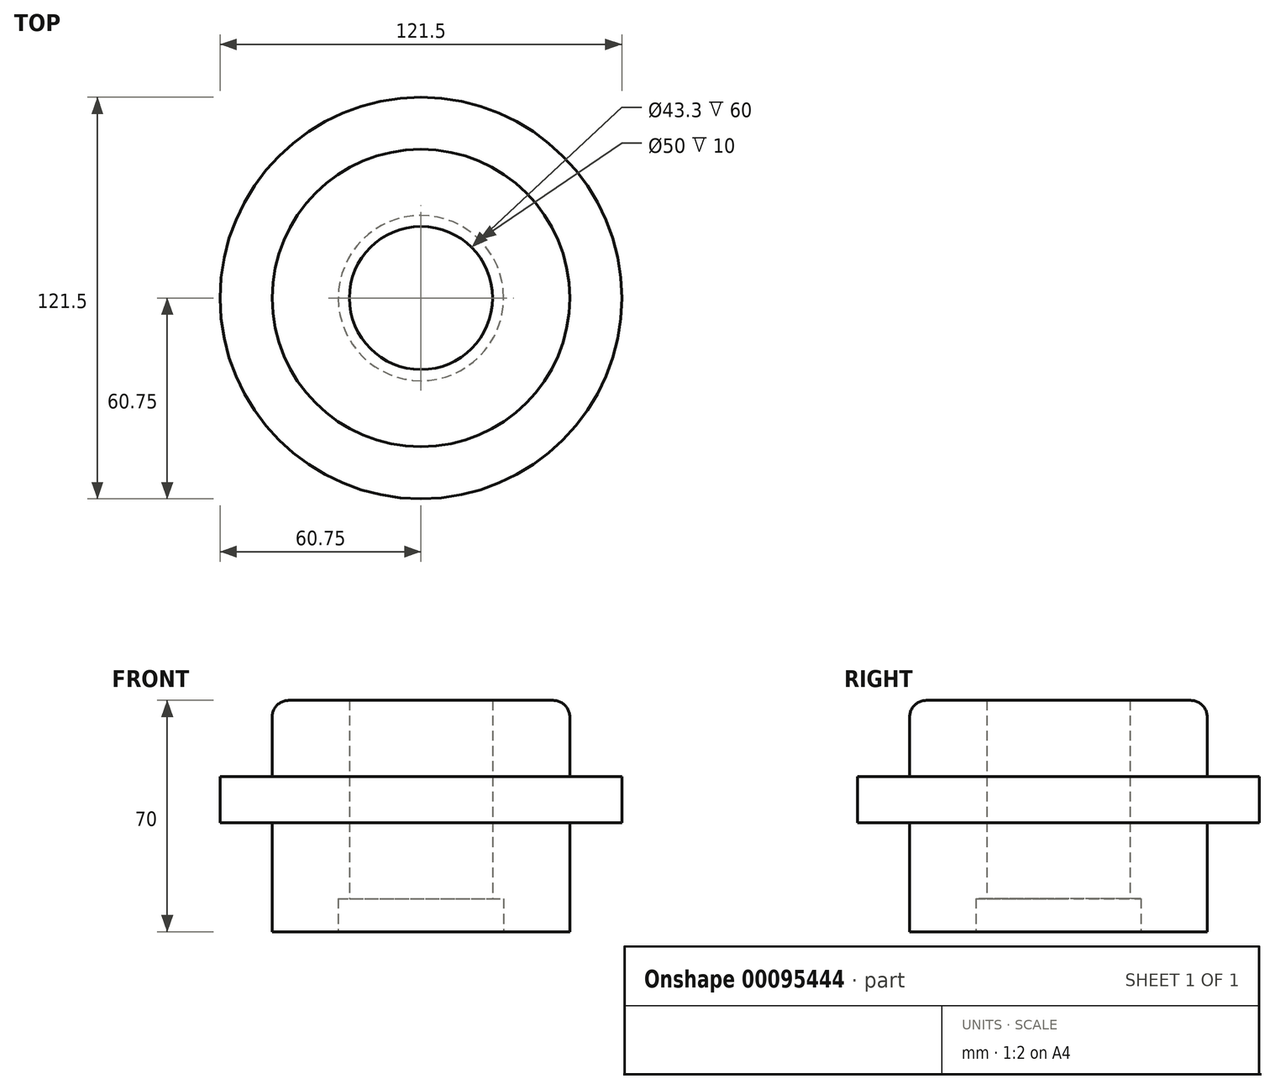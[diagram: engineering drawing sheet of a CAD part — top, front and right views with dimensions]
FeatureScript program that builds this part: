
annotation { "Feature Type Name" : "Feature", "Feature Type Description" : "" }
export const myFeature = defineFeature(function(context is Context, id is Id, definition is map)
    precondition{}
    {
        {
            var Q0;
            Q0=qCreatedBy(makeId("Front.planeOp"),FACE);
            var sketch = newSketch(context, id + "F0", { "sketchPlane" : qUnion([Q0])});
            skLineSegment(sketch, "E0", {"start": v(-60.75, 0) * mm, "end": v(-60.75, 14) * mm});
            skLineSegment(sketch, "E1", {"start": v(-60.75, 14) * mm, "end": v(-45, 14) * mm});
            skLineSegment(sketch, "E2", {"start": v(-45, 14) * mm, "end": v(-45, 37) * mm});
            skLineSegment(sketch, "E3", {"start": v(-45, 37) * mm, "end": v(-21.65, 37) * mm});
            skLineSegment(sketch, "E4", {"start": v(-21.65, 37) * mm, "end": v(-21.65, -33) * mm});
            skLineSegment(sketch, "E5", {"start": v(-21.65, -33) * mm, "end": v(-45, -33) * mm});
            skLineSegment(sketch, "E6", {"start": v(-45, -33) * mm, "end": v(-45, 0) * mm});
            skLineSegment(sketch, "E7", {"start": v(-45, 0) * mm, "end": v(-60.75, 0) * mm});
            skLineSegment(sketch, "E8", {"start": v(0, 0) * mm, "end": v(0, 56.62) * mm, "construction": true});
            skSolve(sketch);
        }
        {
            var Q0;
            Q0=makeQuery(id+"F0.imprint","IMPRINT",FACE,{"disambiguationData":[TD([[makeQuery(id+"F0.imprint","IMPRINT",EDGE,{"derivedFrom":sQuery(id+"F0.wireOp",EDGE,"E0")}),-1.0]])]});
            var Q1;
            Q1=sQuery(id+"F0.wireOp",EDGE,"E8");
            revolve(context, id + "F1", {"entities" : qUnion([Q0]), "axis" : qUnion([Q1]), "revolveType" : RevolveType.FULL});
        }
        {
            var Q0;
            Q0=makeQuery(id+"F1.opRevolve","SWEPT_EDGE",EDGE,{"disambiguationData":[OSD([sQuery(id+"F0.wireOp",EDGE,"E2"),sQuery(id+"F0.wireOp",EDGE,"E3")])]});
            fillet(context, id + "F2", {"entities" : qUnion([Q0]), "radius" : 5 * mm, "tangentPropagation" : true, "allowEdgeOverflow" : false});
        }
        {
            var Q0;
            Q0=makeQuery(id+"F1.opRevolve","SWEPT_FACE",FACE,{"disambiguationData":[OSD([sQuery(id+"F0.wireOp",EDGE,"E5")])]});
            var sketch = newSketch(context, id + "F3", { "sketchPlane" : qUnion([Q0])});
            skCircle(sketch, "E9", {"center": v(0, 0) * mm, "radius": 25 * mm});
            skSolve(sketch);
        }
        {
            var Q0;
            Q0 = qSketchRegion(id + "F3", true);
            extrude(context, id + "F4", {"entities" : qUnion([Q0]), "operationType" : NewBodyOperationType.REMOVE, "oppositeDirection" : true, "depth" : 10 * mm});
        }
    });
